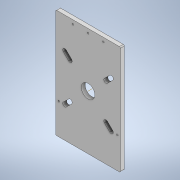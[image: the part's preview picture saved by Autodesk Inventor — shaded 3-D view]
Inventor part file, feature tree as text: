
AUTODESK INVENTOR PART (.ipt)
format: ipt  version: 2021.2 (Build 252289000, 289)  size: 162,304 bytes
history: native  units: in
note: dims shown in document units (in); Inventor stores cm internally (conversion verified against a paired STEP export)
features: sketch x5, extrude x3, hole x2, fillet x1, pattern_circular x1
ambient origin geometry x8: Origin, YZ Plane, XZ Plane, XY Plane, X Axis, Y Axis, Z Axis, Center Point
bodies: Solid1 (feature_tree)
feature tree (12):
  extrude  "Extrusion1"  Depth=7.0in
  extrude  "CenterHole"  Depth=0.25in
  hole  "TopThreeHoles"  [1 undecoded]
  hole  "BottomTwoHoles"  [1 undecoded]
  fillet  "Fillet1"  Radius=5.0in
  extrude  "SlotForScrews"  Depth=1.633in
  pattern_circular  "Circular Pattern1"  [2 undecoded]
  sketch  "Sketch2"  dims[d0=4.1732in d1=7.0in]
  sketch  "Sketch5"  dims[d2=0.25in d3=0.0in d26=0.875in]
  sketch  "Sketch6"  dims[d27=0.0in d28=0.0in d29=0.2559in]
  sketch  "Sketch7"  dims[d30=0.9843in d31=0.9843in]
  sketch  "Sketch8"  dims[d32=0.104in d33=0.276in d34=0.279in d35=0.25in d36=0.5635in d37=1.0in d38=0.8108in d39=5.0in d40=0.1969in d41=0.1969in d42=0.104in d43=0.276in d44=0.279in d45=0.25in d46=0.5635in d47=1.0in d48=0.8108in d49=0.0625in d50=45.0deg d51=0.266in d53=0.75in d54=0.0in d55=0.0in d56=1.5748in d57=360.0deg d59=0.133in d60=1.633in]
note: 4 required parameter values undecoded (feature->parameter linkage not recoverable at this tier; creation-order binding heuristic only, values carry confidence <= 0.55)
